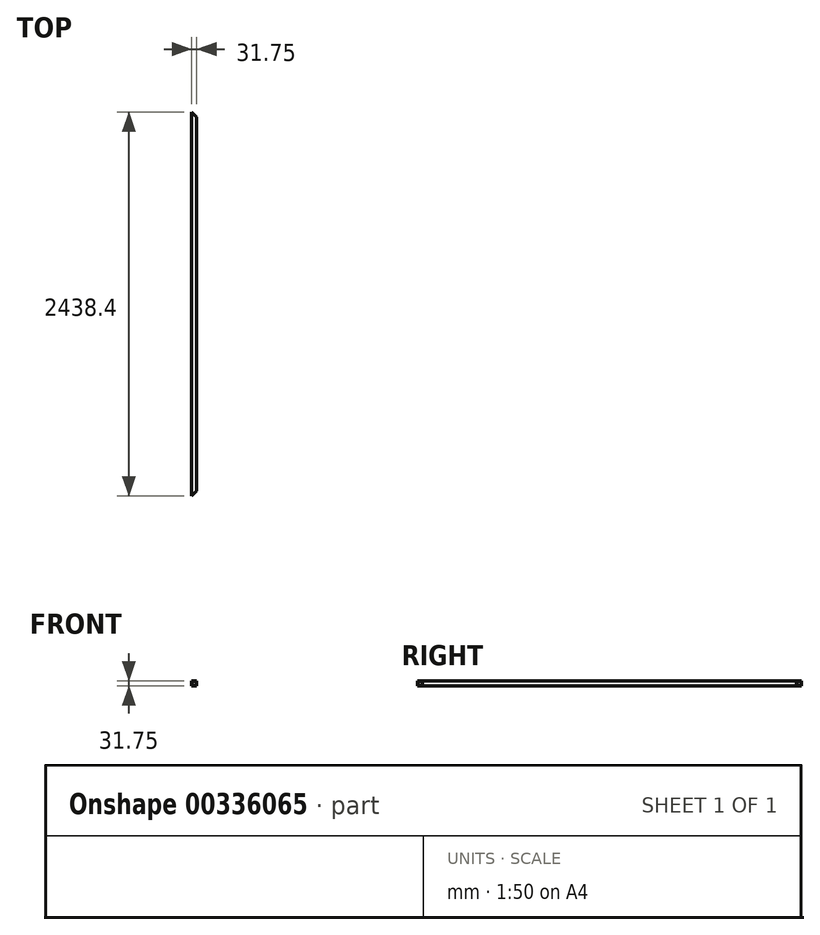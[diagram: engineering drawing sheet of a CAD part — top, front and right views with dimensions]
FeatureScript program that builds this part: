
annotation { "Feature Type Name" : "Feature", "Feature Type Description" : "" }
export const myFeature = defineFeature(function(context is Context, id is Id, definition is map)
    precondition{}
    {
        {
            var Q0;
            Q0=qCreatedBy(makeId("Front.planeOp"),FACE);
            var sketch = newSketch(context, id + "F0", { "sketchPlane" : qUnion([Q0])});
            skLineSegment(sketch, "E0.bottom", {"start": v(-64.17, 32) * mm, "end": v(-32.42, 32) * mm});
            skLineSegment(sketch, "E0.top", {"start": v(-64.17, 0.25) * mm, "end": v(-32.42, 0.25) * mm});
            skLineSegment(sketch, "E0.left", {"start": v(-64.17, 32) * mm, "end": v(-64.17, 0.25) * mm});
            skLineSegment(sketch, "E0.right", {"start": v(-32.42, 32) * mm, "end": v(-32.42, 0.25) * mm});
            skLineSegment(sketch, "E1.0", {"start": v(-34.53, 29.89) * mm, "end": v(-34.53, 2.35) * mm});
            skLineSegment(sketch, "E1.1", {"start": v(-62.06, 29.89) * mm, "end": v(-34.53, 29.89) * mm});
            skLineSegment(sketch, "E1.2", {"start": v(-62.06, 29.89) * mm, "end": v(-62.06, 2.35) * mm});
            skLineSegment(sketch, "E1.3", {"start": v(-62.06, 2.35) * mm, "end": v(-34.53, 2.35) * mm});
            skSolve(sketch);
        }
        {
            var Q0;
            Q0=qSketchRegion(id+"F0",true);
            extrude(context, id + "F1", {"entities" : qUnion([Q0]), "depth" : 2438.4 * mm});
        }
        {
            var Q0;
            Q0=makeQuery(id+"F1.opExtrude","SWEPT_FACE",FACE,{"disambiguationData":[OSD([sQuery(id+"F0.wireOp",EDGE,"E0.bottom")])]});
            var sketch = newSketch(context, id + "F2", { "sketchPlane" : qUnion([Q0])});
            skLineSegment(sketch, "E2", {"start": v(-64.17, 0) * mm, "end": v(-32.42, -31.75) * mm});
            skLineSegment(sketch, "E3.MirrorCS", {"start": v(-64.17, -2438.4) * mm, "end": v(-32.39, -2406.62) * mm});
            skSolve(sketch);
        }
        {
            var Q0;
            Q0 = qSketchRegion(id + "F2", true);
            var Q1;
            {var subQ0=sQuery(id+"F2.wireOp",EDGE,"E2");Q1=makeQuery(id+"F2.imprint","IMPRINT",FACE,{"disambiguationData":[TD([[makeQuery(id+"F2.imprint","IMPRINT",EDGE,{"derivedFrom":subQ0}),1.0]])]});}
            var Q2;
            {var subQ0=sQuery(id+"F2.wireOp",EDGE,"E3.MirrorCS");Q2=makeQuery(id+"F2.imprint","IMPRINT",FACE,{"disambiguationData":[TD([[makeQuery(id+"F2.imprint","IMPRINT",EDGE,{"derivedFrom":subQ0}),-1.0]])]});}
            extrude(context, id + "F3", {"entities" : qUnion([Q0, Q1, Q2]), "operationType" : NewBodyOperationType.REMOVE, "oppositeDirection" : true, "depth" : 76.2 * mm});
        }
    });
